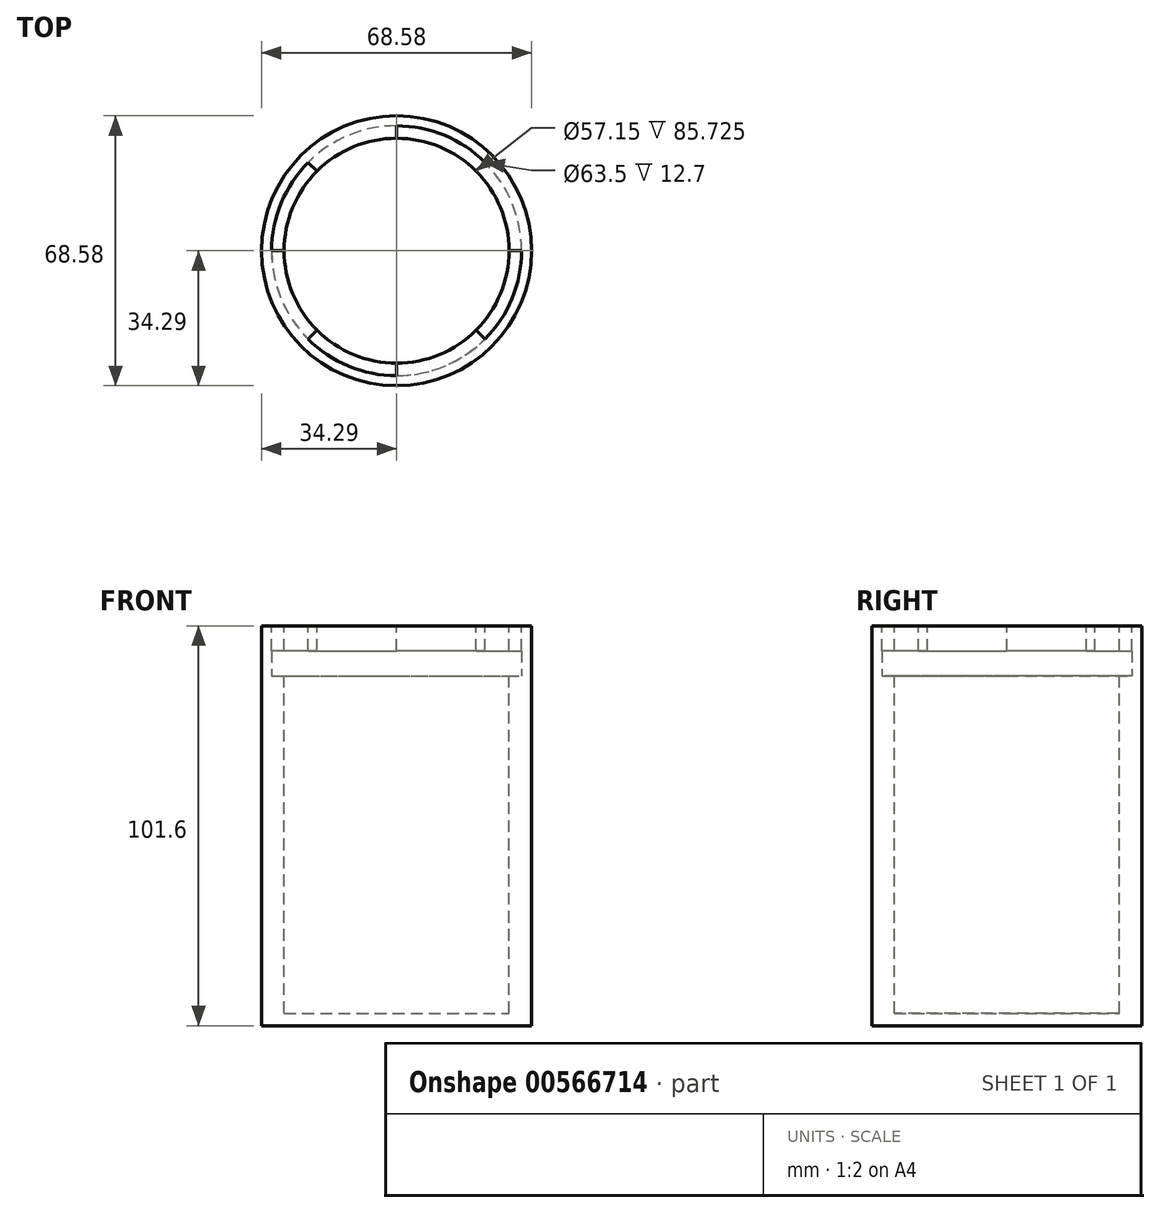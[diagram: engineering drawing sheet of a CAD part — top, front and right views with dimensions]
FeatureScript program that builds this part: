
annotation { "Feature Type Name" : "Feature", "Feature Type Description" : "" }
export const myFeature = defineFeature(function(context is Context, id is Id, definition is map)
    precondition{}
    {
        {
            var Q0;
            Q0=qCreatedBy(makeId("Top.planeOp"),FACE);
            var sketch = newSketch(context, id + "F0", { "sketchPlane" : qUnion([Q0])});
            skCircle(sketch, "E0", {"center": v(0, 0) * mm, "radius": 28.58 * mm});
            skCircle(sketch, "E1", {"center": v(0, 0) * mm, "radius": 34.3 * mm});
            skSolve(sketch);
        }
        {
            var Q0;
            Q0=makeQuery(id+"F0.imprint","IMPRINT",FACE,{"disambiguationData":[TD([[makeQuery(id+"F0.imprint","IMPRINT",EDGE,{"derivedFrom":sQuery(id+"F0.wireOp",EDGE,"E0")}),-1.0]])]});
            extrude(context, id + "F1", {"entities" : qUnion([Q0]), "oppositeDirection" : true, "depth" : 101.6 * mm, "offsetDistance" : 25.4 * mm});
        }
        {
            var Q0;
            Q0=qCreatedBy(makeId("Front.planeOp"),FACE);
            var sketch = newSketch(context, id + "F2", { "sketchPlane" : qUnion([Q0])});
            skLineSegment(sketch, "E2", {"start": v(0, 0) * mm, "end": v(0, -6.35) * mm});
            skLineSegment(sketch, "E3", {"start": v(0, -6.35) * mm, "end": v(-34.3, -6.35) * mm});
            skLineSegment(sketch, "E4", {"start": v(0, -6.35) * mm, "end": v(-28.58, -6.35) * mm});
            skLineSegment(sketch, "E5", {"start": v(-28.58, -6.35) * mm, "end": v(-31.75, -6.35) * mm});
            skLineSegment(sketch, "E6", {"start": v(-28.58, -6.35) * mm, "end": v(-28.58, -12.7) * mm});
            skLineSegment(sketch, "E7", {"start": v(-31.75, -6.35) * mm, "end": v(-31.75, -12.7) * mm});
            skLineSegment(sketch, "E8", {"start": v(-31.75, -12.7) * mm, "end": v(-28.58, -12.7) * mm});
            skSolve(sketch);
        }
        {
            var Q0;
            Q0 = qSketchRegion(id + "F2", true);
            var Q1;
            Q1=sQuery(id+"F2.wireOp",EDGE,"E2");
            revolve(context, id + "F3", {"operationType" : NewBodyOperationType.REMOVE, "entities" : qUnion([Q0]), "axis" : qUnion([Q1]), "revolveType" : RevolveType.FULL, "oppositeDirection" : true});
        }
        {
            var Q0;
            Q0=makeQuery(id+"F1.opExtrude","CAP_FACE",FACE,{"disambiguationData":[OSD([sQuery(id+"F0.wireOp",EDGE,"E0"),sQuery(id+"F0.wireOp",EDGE,"E1")])],"isStart":true});
            var sketch = newSketch(context, id + "F4", { "sketchPlane" : qUnion([Q0])});
            skCircle(sketch, "E9", {"center": v(0, 0) * mm, "radius": 31.75 * mm});
            skLineSegment(sketch, "E10", {"start": v(28.58, 0) * mm, "end": v(31.75, 0) * mm});
            skLineSegment(sketch, "E11", {"start": v(0, 28.58) * mm, "end": v(0, 31.75) * mm});
            skLineSegment(sketch, "E12", {"start": v(-28.58, 0) * mm, "end": v(-31.75, 0) * mm});
            skLineSegment(sketch, "E13", {"start": v(0, 0) * mm, "end": v(0, -31.75) * mm});
            skLineSegment(sketch, "E14", {"start": v(20.2, -20.2) * mm, "end": v(22.45, -22.45) * mm});
            skLineSegment(sketch, "E15", {"start": v(20.2, 20.2) * mm, "end": v(22.45, 22.45) * mm});
            skLineSegment(sketch, "E16", {"start": v(-20.2, 20.2) * mm, "end": v(-22.45, 22.45) * mm});
            skLineSegment(sketch, "E17", {"start": v(-20.2, -20.2) * mm, "end": v(-22.45, -22.45) * mm});
            skArc(sketch, "E18", {"start": v(20.2, 20.2) * mm, "mid": v(10.94, 26.4) * mm, "end": v(0, 28.58) * mm});
            skArc(sketch, "E19.trimOffspring", {"start": v(20.2, -20.2) * mm, "mid": v(26.4, -10.94) * mm, "end": v(28.57, 0) * mm});
            skArc(sketch, "E20.trimOffspring", {"start": v(-20.2, -20.2) * mm, "mid": v(-10.94, -26.4) * mm, "end": v(0, -28.57) * mm});
            skArc(sketch, "E21.trimOffspring", {"start": v(-20.2, 20.2) * mm, "mid": v(-26.4, 10.94) * mm, "end": v(-28.58, 0) * mm});
            skSolve(sketch);
        }
        {
            var Q0;
            {var subQ0=sQuery(id+"F4.wireOp",EDGE,"E11");Q0=makeQuery(id+"F4.imprint","IMPRINT",FACE,{"disambiguationData":[TD([[makeQuery(id+"F4.imprint","IMPRINT",EDGE,{"derivedFrom":subQ0}),-1.0]])]});}
            var Q1;
            {var subQ0=sQuery(id+"F4.wireOp",EDGE,"E12");Q1=makeQuery(id+"F4.imprint","IMPRINT",FACE,{"disambiguationData":[TD([[makeQuery(id+"F4.imprint","IMPRINT",EDGE,{"derivedFrom":subQ0}),-1.0]])]});}
            var Q2;
            {var subQ3=sQuery(id+"F4.wireOp",EDGE,"E17");Q2=makeQuery(id+"F4.imprint","IMPRINT",FACE,{"disambiguationData":[TD([[makeQuery(id+"F4.imprint","IMPRINT",EDGE,{"derivedFrom":subQ3}),1.0]])]});}
            var Q3;
            {var subQ0=sQuery(id+"F4.wireOp",EDGE,"E10");Q3=makeQuery(id+"F4.imprint","IMPRINT",FACE,{"disambiguationData":[TD([[makeQuery(id+"F4.imprint","IMPRINT",EDGE,{"derivedFrom":subQ0}),-1.0]])]});}
            extrude(context, id + "F5", {"entities" : qUnion([Q0, Q1, Q2, Q3]), "operationType" : NewBodyOperationType.REMOVE, "oppositeDirection" : true, "depth" : 6.35 * mm, "offsetDistance" : 25.4 * mm});
        }
        {
            var Q0;
            Q0=makeQuery(id+"F1.opExtrude","CAP_FACE",FACE,{"disambiguationData":[OSD([sQuery(id+"F0.wireOp",EDGE,"E0"),sQuery(id+"F0.wireOp",EDGE,"E1")])],"isStart":false});
            var sketch = newSketch(context, id + "F6", { "sketchPlane" : qUnion([Q0])});
            skCircle(sketch, "E22", {"center": v(0, 0) * mm, "radius": 28.58 * mm});
            skSolve(sketch);
        }
        {
            var Q0;
            Q0 = qSketchRegion(id + "F6", true);
            extrude(context, id + "F7", {"entities" : qUnion([Q0]), "operationType" : NewBodyOperationType.ADD, "oppositeDirection" : true, "depth" : 3.17 * mm, "offsetDistance" : 25.4 * mm});
        }
    });
